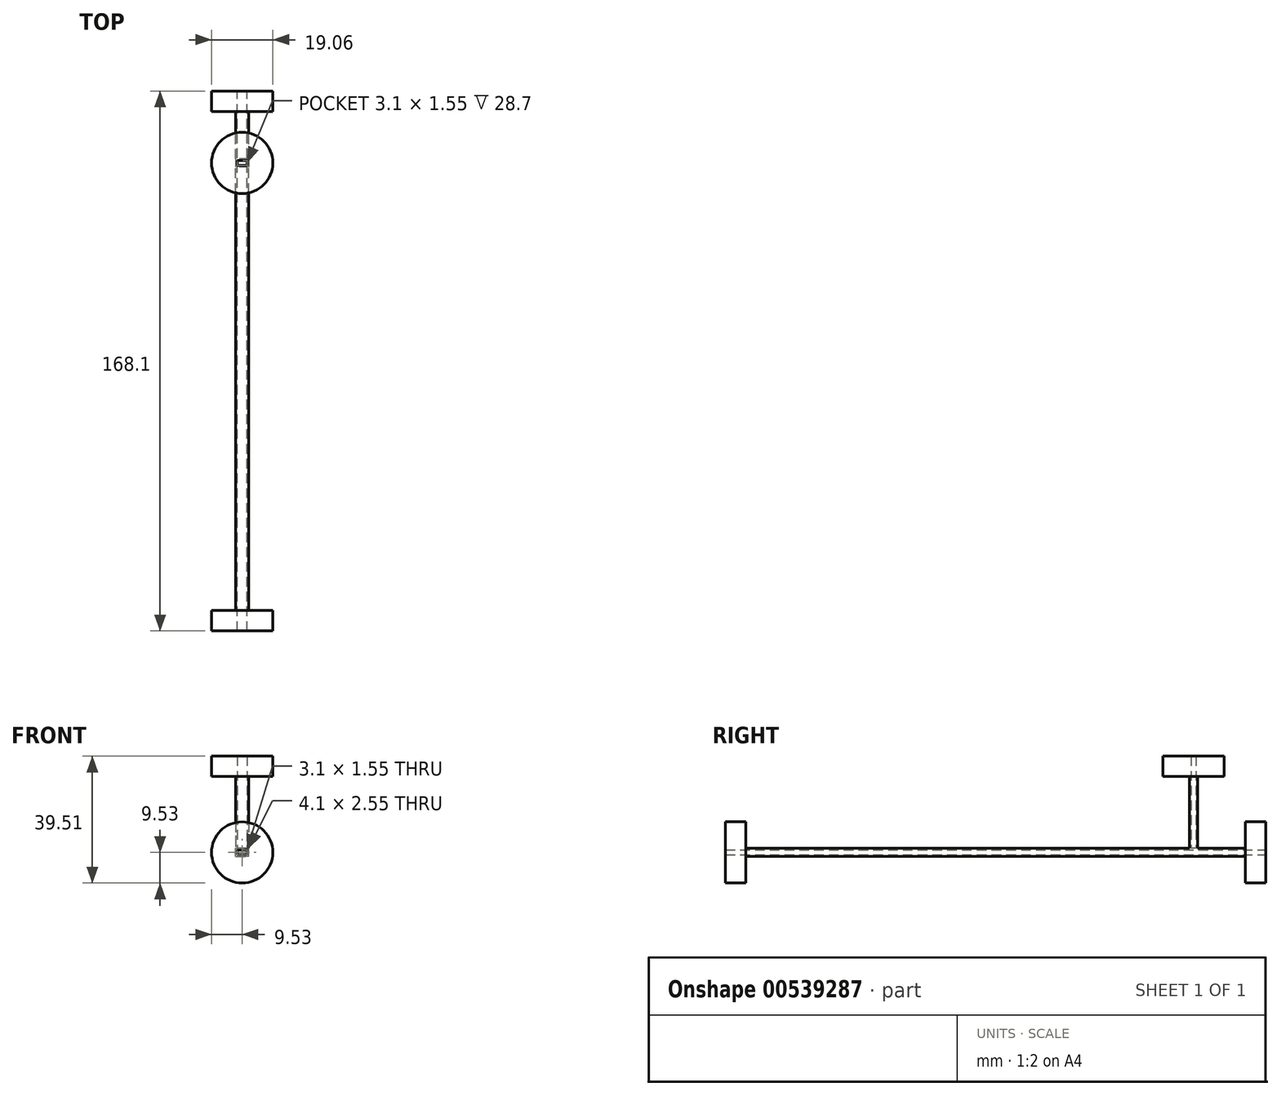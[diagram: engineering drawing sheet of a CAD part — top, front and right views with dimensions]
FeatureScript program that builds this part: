
annotation { "Feature Type Name" : "Feature", "Feature Type Description" : "" }
export const myFeature = defineFeature(function(context is Context, id is Id, definition is map)
    precondition{}
    {
        {
            var Q0;
            Q0=qCreatedBy(makeId("Front.planeOp"),FACE);
            var sketch = newSketch(context, id + "F0", { "sketchPlane" : qUnion([Q0])});
            skLineSegment(sketch, "E0.bottom", {"start": v(-1.55, 0.77) * mm, "end": v(1.55, 0.77) * mm});
            skLineSegment(sketch, "E0.top", {"start": v(-1.55, -0.77) * mm, "end": v(1.55, -0.77) * mm});
            skLineSegment(sketch, "E0.left", {"start": v(-1.55, 0.77) * mm, "end": v(-1.55, -0.77) * mm});
            skLineSegment(sketch, "E0.right", {"start": v(1.55, 0.77) * mm, "end": v(1.55, -0.77) * mm});
            skPoint(sketch, "E0.middle", {"position": v(0, 0) * mm});
            skLineSegment(sketch, "E1.bottom", {"start": v(-2.05, -1.28) * mm, "end": v(2.05, -1.28) * mm});
            skLineSegment(sketch, "E1.top", {"start": v(-2.05, 1.28) * mm, "end": v(2.05, 1.28) * mm});
            skLineSegment(sketch, "E1.left", {"start": v(-2.05, -1.28) * mm, "end": v(-2.05, 1.28) * mm});
            skLineSegment(sketch, "E1.right", {"start": v(2.05, -1.28) * mm, "end": v(2.05, 1.28) * mm});
            skCircle(sketch, "E2", {"center": v(0, 0) * mm, "radius": 9.53 * mm});
            skSolve(sketch);
        }
        {
            assignVariable(context, id + "F1", {"name" : "Length", "anyValue" : 168.1});
        }
        {
            var Q0;
            Q0=makeQuery(id+"F0.imprint","IMPRINT",FACE,{"disambiguationData":[TD([[makeQuery(id+"F0.imprint","IMPRINT",EDGE,{"derivedFrom":sQuery(id+"F0.wireOp",EDGE,"E0.bottom")}),1.0]])]});
            extrude(context, id + "F2", {"entities" : qUnion([Q0]), "depth" : getVariable(context, 'Length') * mm, "offsetDistance" : 25 * mm});
        }
        {
            var Q0;
            Q0=makeQuery(id+"F0.imprint","IMPRINT",FACE,{"disambiguationData":[TD([[makeQuery(id+"F0.imprint","IMPRINT",EDGE,{"derivedFrom":sQuery(id+"F0.wireOp",EDGE,"E1.bottom")}),-1.0]])]});
            extrude(context, id + "F3", {"entities" : qUnion([Q0]), "operationType" : NewBodyOperationType.ADD, "depth" : 6.35 * mm, "offsetDistance" : 25 * mm});
        }
        {
            var Q0;
            Q0=makeQuery(id+"F2.opExtrude","CAP_FACE",FACE,{"disambiguationData":[OSD([sQuery(id+"F0.wireOp",EDGE,"E0.bottom"),sQuery(id+"F0.wireOp",EDGE,"E0.top"),sQuery(id+"F0.wireOp",EDGE,"E0.left"),sQuery(id+"F0.wireOp",EDGE,"E0.right"),sQuery(id+"F0.wireOp",EDGE,"E1.bottom"),sQuery(id+"F0.wireOp",EDGE,"E1.top"),sQuery(id+"F0.wireOp",EDGE,"E1.left"),sQuery(id+"F0.wireOp",EDGE,"E1.right")])],"isStart":false});
            var sketch = newSketch(context, id + "F4", { "sketchPlane" : qUnion([Q0])});
            skCircle(sketch, "E3", {"center": v(0, 0) * mm, "radius": 9.53 * mm});
            skSolve(sketch);
        }
        {
            var Q0;
            Q0=qCreatedBy(makeId("Top.planeOp"),FACE);
            cPlane(context, id + "F5", {"entities" : qUnion([Q0]), "cplaneType" : CPlaneType.OFFSET, "offset" : 1.27 * mm, "width" : 150 * mm, "height" : 150 * mm});
        }
        {
            var Q0;
            Q0=qCreatedBy(id+"F5.planeOp",FACE);
            var sketch = newSketch(context, id + "F6", { "sketchPlane" : qUnion([Q0])});
            skLineSegment(sketch, "E4.bottom", {"start": v(1.55, -21.62) * mm, "end": v(-1.55, -21.62) * mm});
            skLineSegment(sketch, "E4.top", {"start": v(1.55, -23.18) * mm, "end": v(-1.55, -23.18) * mm});
            skLineSegment(sketch, "E4.left", {"start": v(1.55, -21.62) * mm, "end": v(1.55, -23.17) * mm});
            skLineSegment(sketch, "E4.right", {"start": v(-1.55, -21.62) * mm, "end": v(-1.55, -23.17) * mm});
            skPoint(sketch, "E4.middle", {"position": v(0, -22.4) * mm});
            skLineSegment(sketch, "E5.bottom", {"start": v(2.05, -21.12) * mm, "end": v(-2.05, -21.12) * mm});
            skLineSegment(sketch, "E5.top", {"start": v(2.05, -23.67) * mm, "end": v(-2.05, -23.67) * mm});
            skLineSegment(sketch, "E5.left", {"start": v(2.05, -21.12) * mm, "end": v(2.05, -23.67) * mm});
            skLineSegment(sketch, "E5.right", {"start": v(-2.05, -21.12) * mm, "end": v(-2.05, -23.67) * mm});
            skSolve(sketch);
        }
        {
            var Q0;
            Q0=makeQuery(id+"F6.imprint","IMPRINT",FACE,{"disambiguationData":[TD([[makeQuery(id+"F6.imprint","IMPRINT",EDGE,{"derivedFrom":sQuery(id+"F6.wireOp",EDGE,"E4.bottom")}),-1.0]])]});
            extrude(context, id + "F7", {"entities" : qUnion([Q0]), "operationType" : NewBodyOperationType.ADD, "depth" : 28.7 * mm, "offsetDistance" : 25 * mm});
        }
        {
            var Q0;
            Q0=makeQuery(id+"F7.opExtrude","CAP_FACE",FACE,{"disambiguationData":[OSD([sQuery(id+"F6.wireOp",EDGE,"E4.bottom"),sQuery(id+"F6.wireOp",EDGE,"E4.top"),sQuery(id+"F6.wireOp",EDGE,"E4.left"),sQuery(id+"F6.wireOp",EDGE,"E4.right"),sQuery(id+"F6.wireOp",EDGE,"E5.bottom"),sQuery(id+"F6.wireOp",EDGE,"E5.top"),sQuery(id+"F6.wireOp",EDGE,"E5.left"),sQuery(id+"F6.wireOp",EDGE,"E5.right")])],"isStart":false});
            var sketch = newSketch(context, id + "F8", { "sketchPlane" : qUnion([Q0])});
            skLineSegment(sketch, "E6", {"start": v(1.55, -22.4) * mm, "end": v(0, -22.4) * mm});
            skLineSegment(sketch, "E7", {"start": v(0, -22.4) * mm, "end": v(0, -23.18) * mm});
            skCircle(sketch, "E8", {"center": v(0, -22.4) * mm, "radius": 9.53 * mm});
            skSolve(sketch);
        }
        {
            var Q0;
            Q0=makeQuery(id+"F8.imprint","IMPRINT",FACE,{"disambiguationData":[TD([[makeQuery(id+"F8.imprint","IMPRINT",EDGE,{"derivedFrom":sQuery(id+"F8.wireOp",EDGE,"E8")}),1.0]])]});
            extrude(context, id + "F9", {"entities" : qUnion([Q0]), "operationType" : NewBodyOperationType.ADD, "oppositeDirection" : true, "depth" : 6.35 * mm, "offsetDistance" : 25 * mm});
        }
        {
            var Q0;
            Q0=makeQuery(id+"F4.imprint","IMPRINT",FACE,{"disambiguationData":[TD([[makeQuery(id+"F4.imprint","IMPRINT",EDGE,{"derivedFrom":sQuery(id+"F4.wireOp",EDGE,"E3")}),1.0]])]});
            extrude(context, id + "F10", {"entities" : qUnion([Q0]), "operationType" : NewBodyOperationType.ADD, "oppositeDirection" : true, "depth" : 6.35 * mm, "offsetDistance" : 25 * mm});
        }
    });
